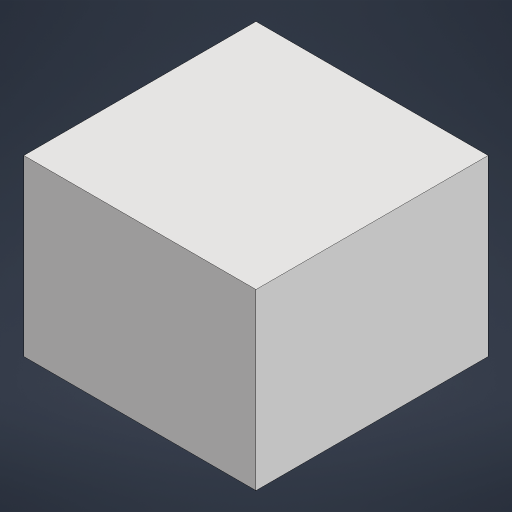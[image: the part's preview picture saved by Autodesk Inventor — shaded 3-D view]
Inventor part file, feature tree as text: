
AUTODESK INVENTOR PART (.ipt)
format: ipt  version: 2023.1 (Build 271208000, 208)  size: 125,952 bytes
history: native  units: in
note: dims shown in document units (in); Inventor stores cm internally (conversion verified against a paired STEP export)
features: extrude x1, sketch x1
ambient origin geometry x8: Origin, YZ Plane, XZ Plane, XY Plane, X Axis, Y Axis, Z Axis, Center Point
bodies: Solid1 (feature_tree)
feature tree (2):
  extrude  "Extrusion1"  Depth=4.0in
  sketch  "Sketch2"  dims[d3=4.0in d4=4.0in d5=3.0in d6=0.0in]
